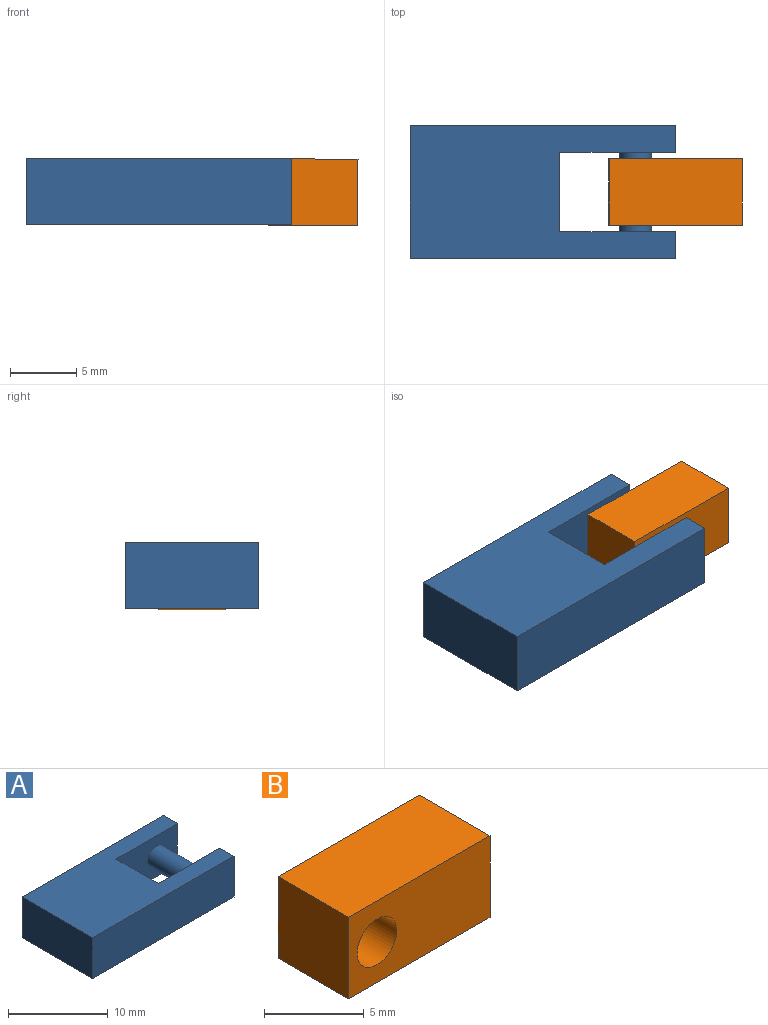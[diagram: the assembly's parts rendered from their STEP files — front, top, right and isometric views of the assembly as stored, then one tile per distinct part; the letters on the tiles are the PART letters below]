
ASSEMBLY  parts=2 mates=1
PART A: 11 faces, bbox 20x10x5 mm
  f0: plane 5x2mm, normal (1,0,0), area 10mm2, adj f1,f4,f6,f9
  f1: plane 20x10mm, normal (0,0,-1), area 147.8mm2, adj f0,f2,f3,f4,f5,f7,f8,f9
  f2: plane 20x5mm, normal (0,1,0), area 100mm2, adj f1,f3,f5,f6
  f3: plane 10x5mm, normal (-1,0,0), area 50mm2, adj f1,f2,f4,f6
  f4: plane 20x5mm, normal (0,-1,0), area 100mm2, adj f0,f1,f3,f6
  f5: plane 5x2mm, normal (1,0,0), area 10mm2, adj f1,f2,f6,f7
  f6: plane 20x10mm, normal (0,0,1), area 147.8mm2, adj f0,f2,f3,f4,f5,f7,f8,f9
  f7: plane 8.71x5mm, normal (0,-1,0), area 38.9mm2, adj f1,f5,f6,f8,f10
  f8: plane 6x5mm, normal (1,0,0), area 30mm2, adj f1,f6,f7,f9
  f9: plane 8.71x5mm, normal (0,1,0), area 38.9mm2, adj f0,f1,f6,f8,f10
  f10: cylinder r=1.22mm len=6mm, axis (0,1,0), area 46mm2, adj f7,f9
PART B: 7 faces, bbox 10x5x5 mm
  f0: plane 10x5mm, normal (0,1,0), area 43.8mm2, adj f1,f3,f4,f5,f6
  f1: plane 5x5mm, normal (-1,0,0), area 25mm2, adj f0,f2,f4,f5
  f2: plane 10x5mm, normal (0,-1,0), area 43.8mm2, adj f1,f3,f4,f5,f6
  f3: plane 5x5mm, normal (1,0,0), area 25mm2, adj f0,f2,f4,f5
  f4: plane 10x5mm, normal (0,0,1), area 50mm2, adj f0,f1,f2,f3
  f5: plane 10x5mm, normal (0,0,-1), area 50mm2, adj f0,f1,f2,f3
  f6: cylinder r=1.4mm len=5mm, axis (0,-1,0), area 44mm2, adj f0,f2
PLACE A rot(axis=(0,0,-1),0deg) t=(11.89,-1.67,-1.73)mm fixed
PLACE B rot(axis=(0,1,0),0.4deg) t=(6.61,-1.43,-1.9)mm
MATE pin_slot A.f10 <-> B.f6  axis (0,1,0) through (-16.87,0.12,0.77)mm
